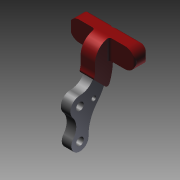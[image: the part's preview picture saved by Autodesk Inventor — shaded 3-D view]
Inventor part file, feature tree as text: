
AUTODESK INVENTOR PART (.ipt)
format: ipt  version: 2011 SP1 (Build 150282100, 282)  size: 215,552 bytes
history: native  units: mm
features: other x21, sketch x7, extrude x5, revolve x2
ambient origin geometry x8: Origin, YZ Plane, XZ Plane, XY Plane, X Axis, Y Axis, Z Axis, Center Point
bodies: Solid1 (feature_tree)
feature tree (35):
  extrude  "Extrusion1"  Depth=6.0mm TaperAngle=0.0deg
  extrude  "Extrusion2"  TaperAngle=360.0deg  [1 undecoded]
  revolve  "Revolution1"  [1 undecoded]
  revolve  "Revolution2"  [1 undecoded]
  extrude  "Extrusion3"  [1 undecoded]
  extrude  "Extrusion4"  [1 undecoded]
  extrude  "Extrusion5"  [1 undecoded]
  other  "HG1_XY"
  other  "HG1_YZ"
  other  "HG1_ZX"
  other  "HG1_X"
  other  "HG1_Y"
  other  "HG1_Z"
  other  "HG1_Center"
  other  "HG2_XY"
  other  "HG2_YZ"
  other  "HG2_ZX"
  other  "HG2_X"
  other  "HG2_Y"
  other  "HG2_Z"
  other  "HG2_Center"
  other  "HG3_XY"
  other  "HG3_YZ"
  other  "HG3_ZX"
  other  "HG3_X"
  other  "HG3_Y"
  other  "HG3_Z"
  other  "HG3_Center"
  sketch  "Skizze_4"
  sketch  "Sketch_1"  dims[d0=4.0mm d1=0.0mm d2=6.0mm d3=0.0mm]
  sketch  "Skizze_5_ALT_Drilling_1"  dims[d4=360.0deg d5=360.0deg]
  sketch  "Skizze_6_ALT_Drilling_2"  dims[d6=6.1mm d7=0.0mm d8=40.0mm d9=0.0mm]
  sketch  "Sketch_2"  dims[d10=10.0mm d11=0.0mm]
  sketch  "Sketch_3"
  sketch  "Sketch_4"
note: 6 required parameter values undecoded (feature->parameter linkage not recoverable at this tier; creation-order binding heuristic only, values carry confidence <= 0.55)